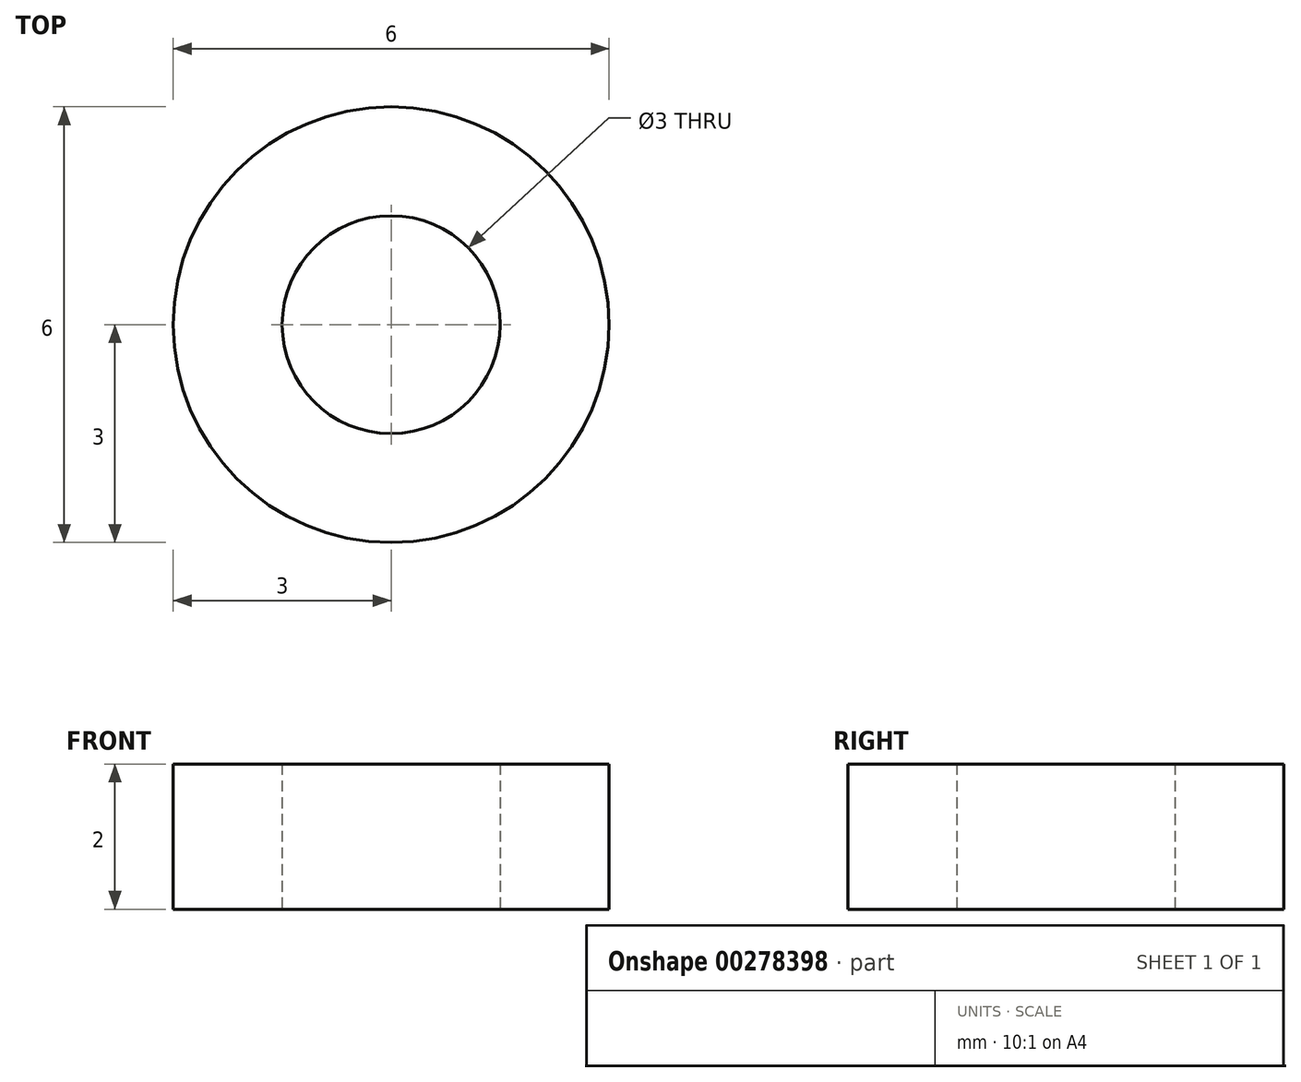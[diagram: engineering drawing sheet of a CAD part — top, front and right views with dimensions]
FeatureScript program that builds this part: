
annotation { "Feature Type Name" : "Feature", "Feature Type Description" : "" }
export const myFeature = defineFeature(function(context is Context, id is Id, definition is map)
    precondition{}
    {
        {
            var Q0;
            Q0=qCreatedBy(makeId("Top.planeOp"),FACE);
            var sketch = newSketch(context, id + "F0", { "sketchPlane" : qUnion([Q0])});
            skCircle(sketch, "E0", {"center": v(0, 0) * mm, "radius": 1.5 * mm});
            skCircle(sketch, "E1", {"center": v(0, 0) * mm, "radius": 3 * mm});
            skSolve(sketch);
        }
        {
            var Q0;
            Q0=makeQuery(id+"F0.imprint","IMPRINT",FACE,{"disambiguationData":[TD([[makeQuery(id+"F0.imprint","IMPRINT",EDGE,{"derivedFrom":sQuery(id+"F0.wireOp",EDGE,"E0")}),-1.0]])]});
            extrude(context, id + "F1", {"entities" : qUnion([Q0]), "depth" : 2 * mm});
        }
    });
